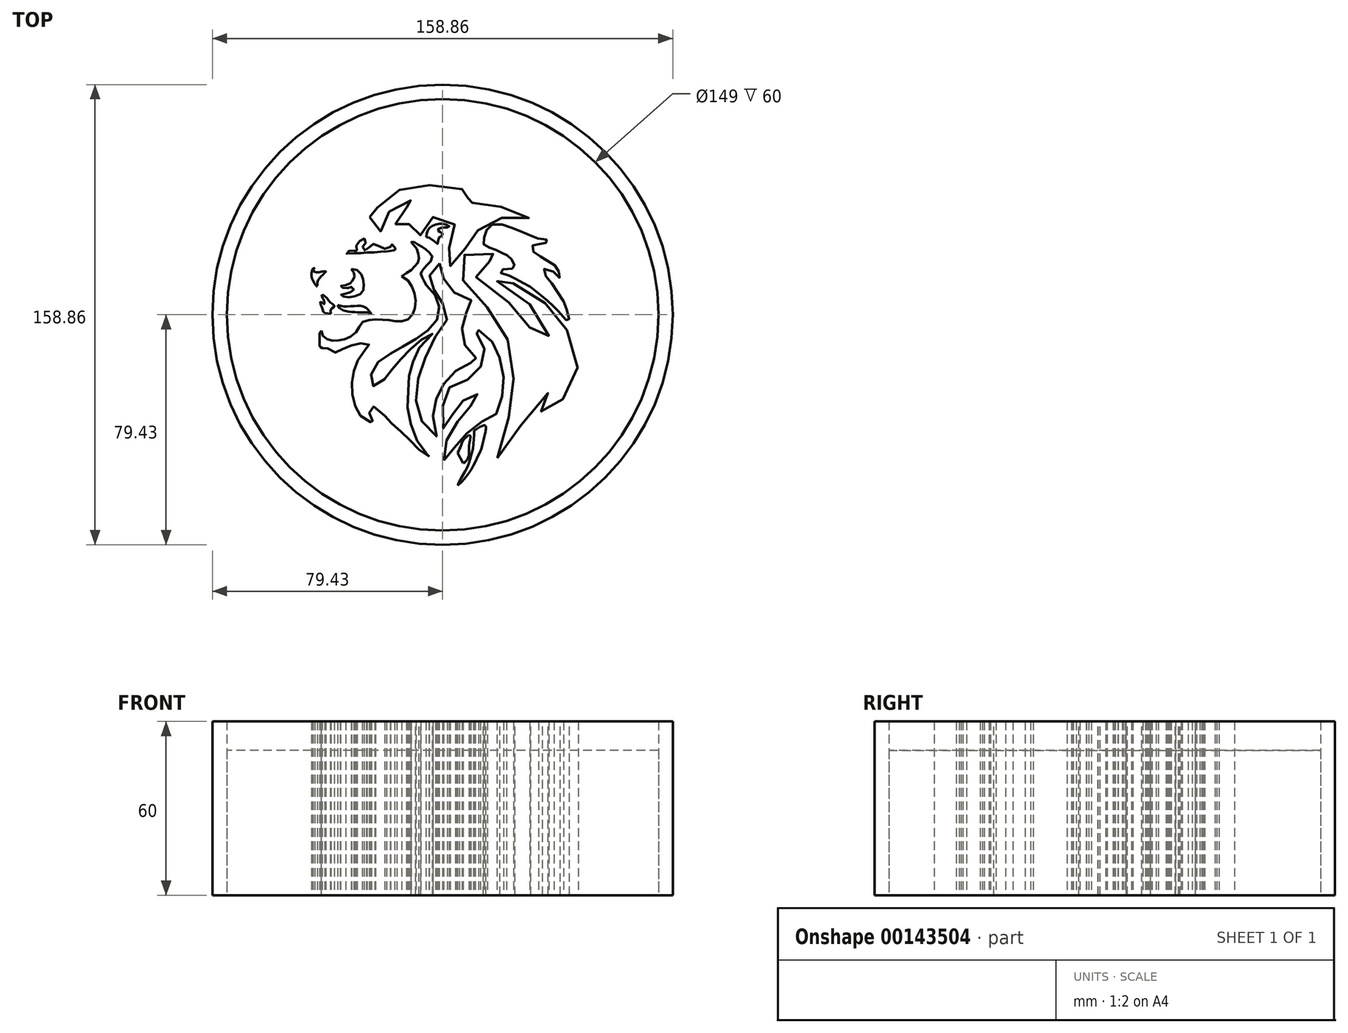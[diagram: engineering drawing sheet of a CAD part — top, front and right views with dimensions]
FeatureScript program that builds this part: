
annotation { "Feature Type Name" : "Feature", "Feature Type Description" : "" }
export const myFeature = defineFeature(function(context is Context, id is Id, definition is map)
    precondition{}
    {
        {
            var Q0;
            Q0=qCreatedBy(makeId("Top.planeOp"),FACE);
            var sketch = newSketch(context, id + "F0", { "sketchPlane" : qUnion([Q0])});
            skCircle(sketch, "E0", {"center": v(0, 0) * mm, "radius": 74.5 * mm});
            skCircle(sketch, "E1", {"center": v(0, 0) * mm, "radius": 79.43 * mm});
            skSolve(sketch);
        }
        {
            var Q0;
            Q0=makeQuery(id+"F0.imprint","IMPRINT",FACE,{"disambiguationData":[TD([[makeQuery(id+"F0.imprint","IMPRINT",EDGE,{"derivedFrom":sQuery(id+"F0.wireOp",EDGE,"E0")}),1.0]])]});
            var sketch = newSketch(context, id + "F1", { "sketchPlane" : qUnion([Q0])});
            skPoint(sketch, "E2", {"position": v(-26.29, 25.3) * mm});
            skPoint(sketch, "E3", {"position": v(-27.08, 24.28) * mm});
            skPoint(sketch, "E4", {"position": v(-27.66, 23.4) * mm});
            skPoint(sketch, "E5", {"position": v(-27.51, 22.47) * mm});
            skPoint(sketch, "E6", {"position": v(-26.13, 22.33) * mm});
            skPoint(sketch, "E7", {"position": v(-25.18, 23.42) * mm});
            skPoint(sketch, "E8", {"position": v(-24.17, 24.44) * mm});
            skPoint(sketch, "E9", {"position": v(-22.71, 24.09) * mm});
            skPoint(sketch, "E10", {"position": v(-20.89, 23.22) * mm});
            skPoint(sketch, "E11", {"position": v(-19.43, 22.72) * mm});
            skPoint(sketch, "E12", {"position": v(-17.97, 23.53) * mm});
            skPoint(sketch, "E13", {"position": v(-17.97, 24.4) * mm});
            skPoint(sketch, "E14", {"position": v(-17.1, 23.97) * mm});
            skPoint(sketch, "E15", {"position": v(-16.44, 23.02) * mm});
            skPoint(sketch, "E16", {"position": v(-15.71, 22.66) * mm});
            skPoint(sketch, "E17", {"position": v(-17.38, 22.15) * mm});
            skPoint(sketch, "E18", {"position": v(-19.57, 21.92) * mm});
            skPoint(sketch, "E19", {"position": v(-21.39, 21.77) * mm});
            skPoint(sketch, "E20", {"position": v(-23.43, 21.54) * mm});
            skPoint(sketch, "E21", {"position": v(-25.83, 21.53) * mm});
            skPoint(sketch, "E22", {"position": v(-27.8, 21.3) * mm});
            skPoint(sketch, "E23", {"position": v(-29.54, 21.22) * mm});
            skPoint(sketch, "E24", {"position": v(-31.73, 21.2) * mm});
            skPoint(sketch, "E25", {"position": v(-33.48, 21.2) * mm});
            skPoint(sketch, "E26", {"position": v(-31.73, 22.16) * mm});
            skPoint(sketch, "E27", {"position": v(-29.55, 22.24) * mm});
            skPoint(sketch, "E28", {"position": v(-29.85, 23.47) * mm});
            skPoint(sketch, "E29", {"position": v(-29.2, 24.78) * mm});
            skPoint(sketch, "E30", {"position": v(-28.04, 25.95) * mm});
            skPoint(sketch, "E31", {"position": v(-26.95, 26.32) * mm});
            skFitSpline(sketch, "E32", {"points": [v(-26.95, 26.32) * mm, v(-26.29, 25.3) * mm, v(-27.08, 24.28) * mm, v(-27.66, 23.4) * mm, v(-27.51, 22.47) * mm, v(-26.13, 22.33) * mm, v(-25.18, 23.42) * mm, v(-24.17, 24.44) * mm, v(-22.71, 24.09) * mm, v(-20.89, 23.22) * mm, v(-19.43, 22.72) * mm, v(-17.97, 23.53) * mm, v(-17.97, 24.4) * mm, v(-17.1, 23.97) * mm, v(-16.44, 23.02) * mm, v(-15.71, 22.66) * mm, v(-17.38, 22.15) * mm, v(-19.57, 21.92) * mm, v(-21.39, 21.77) * mm, v(-23.43, 21.54) * mm, v(-25.83, 21.53) * mm, v(-27.8, 21.3) * mm, v(-29.54, 21.22) * mm, v(-31.73, 21.2) * mm, v(-33.48, 21.2) * mm, v(-31.73, 22.16) * mm, v(-29.55, 22.24) * mm, v(-29.85, 23.47) * mm, v(-29.2, 24.78) * mm, v(-28.04, 25.95) * mm, v(-26.95, 26.32) * mm]});
            skPoint(sketch, "E33", {"position": v(-31.49, 15.76) * mm});
            skPoint(sketch, "E34", {"position": v(-29.68, 15.5) * mm});
            skPoint(sketch, "E35", {"position": v(-28.25, 14.2) * mm});
            skPoint(sketch, "E36", {"position": v(-27.6, 12.78) * mm});
            skPoint(sketch, "E37", {"position": v(-27.15, 11.31) * mm});
            skPoint(sketch, "E38", {"position": v(-27.25, 9.4) * mm});
            skPoint(sketch, "E39", {"position": v(-27.79, 7.88) * mm});
            skPoint(sketch, "E40", {"position": v(-28.82, 6.84) * mm});
            skPoint(sketch, "E41", {"position": v(-30.73, 6.28) * mm});
            skPoint(sketch, "E42", {"position": v(-32.75, 6.06) * mm});
            skPoint(sketch, "E43", {"position": v(-34.44, 6.32) * mm});
            skPoint(sketch, "E44", {"position": v(-35.15, 6.7) * mm});
            skPoint(sketch, "E45", {"position": v(-34.28, 7.25) * mm});
            skPoint(sketch, "E46", {"position": v(-33.03, 7.25) * mm});
            skPoint(sketch, "E47", {"position": v(-31.66, 7.8) * mm});
            skPoint(sketch, "E48", {"position": v(-30.8, 8.52) * mm});
            skPoint(sketch, "E49", {"position": v(-30.69, 9.12) * mm});
            skPoint(sketch, "E50", {"position": v(-31.5, 9.6) * mm});
            skPoint(sketch, "E51", {"position": v(-32.33, 9.27) * mm});
            skPoint(sketch, "E52", {"position": v(-33.47, 9.21) * mm});
            skPoint(sketch, "E53", {"position": v(-34.56, 9.37) * mm});
            skPoint(sketch, "E54", {"position": v(-35.27, 9.86) * mm});
            skPoint(sketch, "E55", {"position": v(-34.3, 10.19) * mm});
            skPoint(sketch, "E56", {"position": v(-33.1, 10.3) * mm});
            skPoint(sketch, "E57", {"position": v(-31.9, 10.85) * mm});
            skPoint(sketch, "E58", {"position": v(-31.3, 11.51) * mm});
            skPoint(sketch, "E59", {"position": v(-30.7, 12.28) * mm});
            skPoint(sketch, "E60", {"position": v(-30.43, 13.26) * mm});
            skPoint(sketch, "E61", {"position": v(-30.44, 13.97) * mm});
            skPoint(sketch, "E62", {"position": v(-30.93, 14.94) * mm});
            skPoint(sketch, "E63", {"position": v(-36.17, 3.32) * mm});
            skPoint(sketch, "E64", {"position": v(-35.08, 3) * mm});
            skPoint(sketch, "E65", {"position": v(-33.6, 2.84) * mm});
            skPoint(sketch, "E66", {"position": v(-32.13, 2.96) * mm});
            skPoint(sketch, "E67", {"position": v(-30.5, 3.02) * mm});
            skPoint(sketch, "E68", {"position": v(-28.91, 3.19) * mm});
            skPoint(sketch, "E69", {"position": v(-27.77, 3.03) * mm});
            skPoint(sketch, "E70", {"position": v(-26.56, 2.44) * mm});
            skPoint(sketch, "E71", {"position": v(-25.8, 1.79) * mm});
            skPoint(sketch, "E72", {"position": v(-25.14, 1.14) * mm});
            skPoint(sketch, "E73", {"position": v(-24.59, 0.49) * mm});
            skPoint(sketch, "E74", {"position": v(-25.85, 0.8) * mm});
            skPoint(sketch, "E75", {"position": v(-27.1, 0.8) * mm});
            skPoint(sketch, "E76", {"position": v(-28.74, 0.85) * mm});
            skPoint(sketch, "E77", {"position": v(-30.05, 0.9) * mm});
            skPoint(sketch, "E78", {"position": v(-31.25, 0.9) * mm});
            skPoint(sketch, "E79", {"position": v(-32.72, 1.16) * mm});
            skPoint(sketch, "E80", {"position": v(-33.98, 1.42) * mm});
            skPoint(sketch, "E81", {"position": v(-35.02, 1.8) * mm});
            skPoint(sketch, "E82", {"position": v(-37.32, 3.03) * mm});
            skPoint(sketch, "E83", {"position": v(-38.03, 3.7) * mm});
            skPoint(sketch, "E84", {"position": v(-38.85, 4.34) * mm});
            skPoint(sketch, "E85", {"position": v(-39.57, 5.32) * mm});
            skPoint(sketch, "E86", {"position": v(-40.22, 6.02) * mm});
            skPoint(sketch, "E87", {"position": v(-41, 6.62) * mm});
            skPoint(sketch, "E88", {"position": v(-41.6, 7) * mm});
            skPoint(sketch, "E89", {"position": v(-41.59, 6.02) * mm});
            skPoint(sketch, "E90", {"position": v(-40.93, 5.2) * mm});
            skPoint(sketch, "E91", {"position": v(-40.76, 4.17) * mm});
            skPoint(sketch, "E92", {"position": v(-40.76, 3.68) * mm});
            skPoint(sketch, "E93", {"position": v(-41.58, 4.17) * mm});
            skPoint(sketch, "E94", {"position": v(-42.13, 4.5) * mm});
            skPoint(sketch, "E95", {"position": v(-42.13, 3.72) * mm});
            skPoint(sketch, "E96", {"position": v(-41.74, 2.76) * mm});
            skPoint(sketch, "E97", {"position": v(-41.47, 2.04) * mm});
            skPoint(sketch, "E98", {"position": v(-41.12, 1.08) * mm});
            skPoint(sketch, "E99", {"position": v(-40.57, 0.53) * mm});
            skPoint(sketch, "E100", {"position": v(-38.5, 0.37) * mm});
            skPoint(sketch, "E101", {"position": v(-38.6, 0.85) * mm});
            skPoint(sketch, "E102", {"position": v(-38.71, 1.47) * mm});
            skPoint(sketch, "E103", {"position": v(-38.61, 1.74) * mm});
            skPoint(sketch, "E104", {"position": v(-38.37, 2.05) * mm});
            skPoint(sketch, "E105", {"position": v(-37.9, 2.43) * mm});
            skPoint(sketch, "E106", {"position": v(-43.32, 9.75) * mm});
            skPoint(sketch, "E107", {"position": v(-43.16, 10.5) * mm});
            skPoint(sketch, "E108", {"position": v(-43.13, 11.43) * mm});
            skPoint(sketch, "E109", {"position": v(-42.79, 12.26) * mm});
            skPoint(sketch, "E110", {"position": v(-42.3, 12.88) * mm});
            skPoint(sketch, "E111", {"position": v(-41.7, 13.46) * mm});
            skPoint(sketch, "E112", {"position": v(-41.18, 13.88) * mm});
            skPoint(sketch, "E113", {"position": v(-40.73, 14.46) * mm});
            skPoint(sketch, "E114", {"position": v(-40.25, 15.01) * mm});
            skPoint(sketch, "E115", {"position": v(-41.08, 15) * mm});
            skPoint(sketch, "E116", {"position": v(-42.14, 14.76) * mm});
            skPoint(sketch, "E117", {"position": v(-43.35, 14.62) * mm});
            skPoint(sketch, "E118", {"position": v(-44.28, 14.86) * mm});
            skPoint(sketch, "E119", {"position": v(-44.7, 15.37) * mm});
            skPoint(sketch, "E120", {"position": v(-44.62, 15.99) * mm});
            skPoint(sketch, "E121", {"position": v(-44.04, 16.37) * mm});
            skPoint(sketch, "E122", {"position": v(-45.04, 15.37) * mm});
            skPoint(sketch, "E123", {"position": v(-45.24, 14.3) * mm});
            skPoint(sketch, "E124", {"position": v(-45.27, 13.24) * mm});
            skPoint(sketch, "E125", {"position": v(-44.92, 12.21) * mm});
            skPoint(sketch, "E126", {"position": v(-44.5, 11.36) * mm});
            skFitSpline(sketch, "E127", {"points": [v(-44.04, 16.37) * mm, v(-44.62, 15.99) * mm, v(-45.04, 15.37) * mm, v(-45.24, 14.3) * mm, v(-45.27, 13.24) * mm, v(-44.92, 12.21) * mm, v(-44.5, 11.36) * mm, v(-43.32, 9.75) * mm, v(-43.16, 10.5) * mm, v(-43.13, 11.43) * mm, v(-42.79, 12.26) * mm, v(-42.3, 12.88) * mm, v(-41.7, 13.46) * mm, v(-41.18, 13.88) * mm, v(-40.73, 14.46) * mm, v(-40.25, 15.01) * mm, v(-41.08, 15) * mm, v(-42.14, 14.76) * mm, v(-43.35, 14.62) * mm, v(-44.28, 14.86) * mm, v(-44.7, 15.37) * mm, v(-44.04, 16.37) * mm]});
            skFitSpline(sketch, "E128", {"points": [v(-31.49, 15.76) * mm, v(-30.93, 14.94) * mm, v(-30.44, 13.97) * mm, v(-30.43, 13.26) * mm, v(-30.7, 12.28) * mm, v(-31.3, 11.51) * mm, v(-31.9, 10.85) * mm, v(-33.1, 10.3) * mm, v(-34.3, 10.19) * mm, v(-35.27, 9.86) * mm, v(-34.56, 9.37) * mm, v(-33.47, 9.21) * mm, v(-32.33, 9.27) * mm, v(-31.5, 9.6) * mm, v(-30.69, 9.12) * mm, v(-30.8, 8.52) * mm, v(-31.66, 7.8) * mm, v(-33.03, 7.25) * mm, v(-34.28, 7.25) * mm, v(-35.15, 6.7) * mm, v(-34.44, 6.32) * mm, v(-32.75, 6.06) * mm, v(-30.73, 6.28) * mm, v(-28.82, 6.84) * mm, v(-27.55, 7.88) * mm, v(-27.25, 9.4) * mm, v(-27.15, 11.31) * mm, v(-27.6, 12.78) * mm, v(-28.25, 14.2) * mm, v(-29.68, 15.5) * mm, v(-31.49, 15.76) * mm]});
            skFitSpline(sketch, "E129", {"points": [v(-38.5, 0.37) * mm, v(-38.6, 0.85) * mm, v(-38.71, 1.47) * mm, v(-38.61, 1.74) * mm, v(-38.37, 2.05) * mm, v(-37.9, 2.43) * mm, v(-37.32, 3.03) * mm, v(-38.03, 3.7) * mm, v(-38.85, 4.34) * mm, v(-39.57, 5.32) * mm, v(-40.22, 6.02) * mm, v(-41, 6.62) * mm, v(-41.6, 7) * mm, v(-41.59, 6.02) * mm, v(-40.93, 5.2) * mm, v(-40.76, 4.17) * mm, v(-40.76, 3.68) * mm, v(-41.58, 4.17) * mm, v(-42.13, 4.5) * mm, v(-42.13, 3.72) * mm, v(-41.74, 2.76) * mm, v(-41.47, 2.04) * mm, v(-41.12, 1.08) * mm, v(-40.57, 0.53) * mm], "startDerivative": vector(-2.7, 13.07) * mm, "endDerivative": vector(14.2, -10.78) * mm});
            skLineSegment(sketch, "E130", {"start": v(-40.57, 0.53) * mm, "end": v(-38.5, 0.37) * mm});
            skFitSpline(sketch, "E131", {"points": [v(-36.17, 3.32) * mm, v(-35.08, 3) * mm, v(-33.6, 2.84) * mm, v(-32.13, 2.96) * mm, v(-30.5, 3.02) * mm, v(-28.91, 3.19) * mm, v(-27.77, 3.03) * mm, v(-26.56, 2.44) * mm, v(-25.8, 1.79) * mm, v(-25.14, 1.14) * mm, v(-24.59, 0.49) * mm, v(-25.85, 0.8) * mm, v(-27.1, 0.8) * mm, v(-28.74, 0.85) * mm, v(-30.05, 0.9) * mm, v(-31.25, 0.9) * mm, v(-32.72, 1.16) * mm, v(-33.98, 1.42) * mm, v(-35.02, 1.8) * mm, v(-36.17, 3.32) * mm]});
            skPoint(sketch, "E132", {"position": v(-41.77, -5.54) * mm});
            skPoint(sketch, "E133", {"position": v(-41.77, -6.47) * mm});
            skPoint(sketch, "E134", {"position": v(-41.15, -7.5) * mm});
            skPoint(sketch, "E135", {"position": v(-40.33, -8.27) * mm});
            skPoint(sketch, "E136", {"position": v(-39.5, -8.63) * mm});
            skPoint(sketch, "E137", {"position": v(-38.27, -8.94) * mm});
            skPoint(sketch, "E138", {"position": v(-37.14, -8.94) * mm});
            skPoint(sketch, "E139", {"position": v(-35.75, -8.89) * mm});
            skPoint(sketch, "E140", {"position": v(-34.56, -8.68) * mm});
            skPoint(sketch, "E141", {"position": v(-33.27, -8.22) * mm});
            skPoint(sketch, "E142", {"position": v(-32.04, -7.65) * mm});
            skPoint(sketch, "E143", {"position": v(-30.7, -6.78) * mm});
            skPoint(sketch, "E144", {"position": v(-29.57, -5.7) * mm});
            skPoint(sketch, "E145", {"position": v(-28.74, -4.25) * mm});
            skPoint(sketch, "E146", {"position": v(-28.48, -2.96) * mm});
            skPoint(sketch, "E147", {"position": v(-27.1, -2.35) * mm});
            skPoint(sketch, "E148", {"position": v(-25.75, -1.88) * mm});
            skPoint(sketch, "E149", {"position": v(-24.2, -1.63) * mm});
            skPoint(sketch, "E150", {"position": v(-22.56, -1.57) * mm});
            skPoint(sketch, "E151", {"position": v(-21.02, -1.68) * mm});
            skPoint(sketch, "E152", {"position": v(-19.37, -1.83) * mm});
            skPoint(sketch, "E153", {"position": v(-17.87, -1.93) * mm});
            skPoint(sketch, "E154", {"position": v(-16.59, -2.14) * mm});
            skPoint(sketch, "E155", {"position": v(-15.1, -2.24) * mm});
            skPoint(sketch, "E156", {"position": v(-13.7, -2.24) * mm});
            skPoint(sketch, "E157", {"position": v(-12.47, -1.88) * mm});
            skPoint(sketch, "E158", {"position": v(-11.18, -0.96) * mm});
            skPoint(sketch, "E159", {"position": v(-10.1, 0.7) * mm});
            skPoint(sketch, "E160", {"position": v(-9.63, 2.08) * mm});
            skPoint(sketch, "E161", {"position": v(-9.38, 3.83) * mm});
            skPoint(sketch, "E162", {"position": v(-9.33, 5.48) * mm});
            skPoint(sketch, "E163", {"position": v(-9.74, 7.34) * mm});
            skPoint(sketch, "E164", {"position": v(-10.4, 9.19) * mm});
            skPoint(sketch, "E165", {"position": v(-11.18, 10.79) * mm});
            skPoint(sketch, "E166", {"position": v(-12.42, 12.23) * mm});
            skPoint(sketch, "E167", {"position": v(-14.12, 13.2) * mm});
            skPoint(sketch, "E168", {"position": v(-12.42, 14.4) * mm});
            skPoint(sketch, "E169", {"position": v(-10.82, 15.47) * mm});
            skPoint(sketch, "E170", {"position": v(-9.48, 16.86) * mm});
            skPoint(sketch, "E171", {"position": v(-8.3, 18.4) * mm});
            skPoint(sketch, "E172", {"position": v(-8.3, 20.37) * mm});
            skPoint(sketch, "E173", {"position": v(-8.66, 22.17) * mm});
            skPoint(sketch, "E174", {"position": v(-9.9, 24.02) * mm});
            skPoint(sketch, "E175", {"position": v(-10.77, 24.9) * mm});
            skPoint(sketch, "E176", {"position": v(-10.66, 25.41) * mm});
            skPoint(sketch, "E177", {"position": v(-9.17, 24.64) * mm});
            skPoint(sketch, "E178", {"position": v(-7.52, 23.76) * mm});
            skPoint(sketch, "E179", {"position": v(-6.13, 22.79) * mm});
            skPoint(sketch, "E180", {"position": v(-4.84, 21.7) * mm});
            skPoint(sketch, "E181", {"position": v(-3.56, 20.26) * mm});
            skPoint(sketch, "E182", {"position": v(-4.28, 18.25) * mm});
            skPoint(sketch, "E183", {"position": v(-5.82, 16.7) * mm});
            skPoint(sketch, "E184", {"position": v(-6.65, 15.73) * mm});
            skPoint(sketch, "E185", {"position": v(-7.37, 14.75) * mm});
            skPoint(sketch, "E186", {"position": v(-7.52, 14.19) * mm});
            skPoint(sketch, "E187", {"position": v(-7.21, 13.3) * mm});
            skPoint(sketch, "E188", {"position": v(-6.54, 11.92) * mm});
            skPoint(sketch, "E189", {"position": v(-5.82, 10.53) * mm});
            skPoint(sketch, "E190", {"position": v(-4.84, 9.34) * mm});
            skPoint(sketch, "E191", {"position": v(-3.5, 7.85) * mm});
            skPoint(sketch, "E192", {"position": v(-2.42, 6.46) * mm});
            skPoint(sketch, "E193", {"position": v(-1.65, 5.17) * mm});
            skPoint(sketch, "E194", {"position": v(-1.14, 3.73) * mm});
            skPoint(sketch, "E195", {"position": v(-1.3, 1.93) * mm});
            skPoint(sketch, "E196", {"position": v(-1.3, -0.39) * mm});
            skPoint(sketch, "E197", {"position": v(-2.17, -2.14) * mm});
            skPoint(sketch, "E198", {"position": v(-3.4, -3.79) * mm});
            skPoint(sketch, "E199", {"position": v(-5.36, -5.6) * mm});
            skPoint(sketch, "E200", {"position": v(-6.9, -6.88) * mm});
            skPoint(sketch, "E201", {"position": v(-9.22, -8.32) * mm});
            skPoint(sketch, "E202", {"position": v(-12.1, -9.97) * mm});
            skPoint(sketch, "E203", {"position": v(-14.06, -11.2) * mm});
            skPoint(sketch, "E204", {"position": v(-16.07, -12.29) * mm});
            skPoint(sketch, "E205", {"position": v(-17.98, -13.42) * mm});
            skPoint(sketch, "E206", {"position": v(-19.93, -14.7) * mm});
            skPoint(sketch, "E207", {"position": v(-22.25, -16.36) * mm});
            skPoint(sketch, "E208", {"position": v(-23.85, -18.47) * mm});
            skPoint(sketch, "E209", {"position": v(-24.67, -20.63) * mm});
            skPoint(sketch, "E210", {"position": v(-24.88, -23.36) * mm});
            skPoint(sketch, "E211", {"position": v(-24.42, -24.5) * mm});
            skPoint(sketch, "E212", {"position": v(-22.77, -24.5) * mm});
            skPoint(sketch, "E213", {"position": v(-21.02, -23.41) * mm});
            skPoint(sketch, "E214", {"position": v(-19.68, -21.6) * mm});
            skPoint(sketch, "E215", {"position": v(-18.65, -20.01) * mm});
            skPoint(sketch, "E216", {"position": v(-17.51, -18.93) * mm});
            skPoint(sketch, "E217", {"position": v(-16.23, -17.54) * mm});
            skPoint(sketch, "E218", {"position": v(-14.73, -15.63) * mm});
            skPoint(sketch, "E219", {"position": v(-12.88, -13.68) * mm});
            skPoint(sketch, "E220", {"position": v(-11.64, -12.34) * mm});
            skPoint(sketch, "E221", {"position": v(-9.94, -10.9) * mm});
            skPoint(sketch, "E222", {"position": v(-7.99, -9.15) * mm});
            skPoint(sketch, "E223", {"position": v(-5.82, -7.7) * mm});
            skPoint(sketch, "E224", {"position": v(-3.3, -6.36) * mm});
            skPoint(sketch, "E225", {"position": v(-6.08, -8.78) * mm});
            skPoint(sketch, "E226", {"position": v(-8.09, -11.46) * mm});
            skPoint(sketch, "E227", {"position": v(-9.22, -13.83) * mm});
            skPoint(sketch, "E228", {"position": v(-10.25, -16.3) * mm});
            skPoint(sketch, "E229", {"position": v(-10.97, -18.62) * mm});
            skPoint(sketch, "E230", {"position": v(-11.64, -21.35) * mm});
            skPoint(sketch, "E231", {"position": v(-11.9, -23.46) * mm});
            skPoint(sketch, "E232", {"position": v(-11.9, -26.7) * mm});
            skPoint(sketch, "E233", {"position": v(-12.2, -29.9) * mm});
            skPoint(sketch, "E234", {"position": v(-11.9, -33.04) * mm});
            skPoint(sketch, "E235", {"position": v(-11.33, -36.34) * mm});
            skPoint(sketch, "E236", {"position": v(-10.4, -39.9) * mm});
            skPoint(sketch, "E237", {"position": v(-8.91, -43.24) * mm});
            skPoint(sketch, "E238", {"position": v(-7.37, -45.92) * mm});
            skPoint(sketch, "E239", {"position": v(-5.62, -47.87) * mm});
            skPoint(sketch, "E240", {"position": v(-4.64, -48.96) * mm});
            skPoint(sketch, "E241", {"position": v(-7.52, -47.1) * mm});
            skPoint(sketch, "E242", {"position": v(-10.51, -44.11) * mm});
            skPoint(sketch, "E243", {"position": v(-13.34, -41.33) * mm});
            skPoint(sketch, "E244", {"position": v(-16.38, -38.5) * mm});
            skPoint(sketch, "E245", {"position": v(-18.6, -36.6) * mm});
            skPoint(sketch, "E246", {"position": v(-20.66, -34.12) * mm});
            skPoint(sketch, "E247", {"position": v(-24.36, -31.7) * mm});
            skPoint(sketch, "E248", {"position": v(-25.24, -33.14) * mm});
            skPoint(sketch, "E249", {"position": v(-25.09, -35.05) * mm});
            skPoint(sketch, "E250", {"position": v(-24.16, -36.75) * mm});
            skPoint(sketch, "E251", {"position": v(-23.39, -37.52) * mm});
            skPoint(sketch, "E252", {"position": v(-26.42, -36.39) * mm});
            skPoint(sketch, "E253", {"position": v(-28.43, -34.69) * mm});
            skPoint(sketch, "E254", {"position": v(-29.82, -32.37) * mm});
            skPoint(sketch, "E255", {"position": v(-30.96, -28.61) * mm});
            skPoint(sketch, "E256", {"position": v(-31.32, -25.57) * mm});
            skPoint(sketch, "E257", {"position": v(-31.16, -21.71) * mm});
            skPoint(sketch, "E258", {"position": v(-30.5, -18.83) * mm});
            skPoint(sketch, "E259", {"position": v(-29.2, -15.63) * mm});
            skPoint(sketch, "E260", {"position": v(-27.2, -12.54) * mm});
            skPoint(sketch, "E261", {"position": v(-24.83, -10.43) * mm});
            skPoint(sketch, "E262", {"position": v(-25.96, -10.28) * mm});
            skPoint(sketch, "E263", {"position": v(-27.3, -9.92) * mm});
            skPoint(sketch, "E264", {"position": v(-29.93, -10.07) * mm});
            skPoint(sketch, "E265", {"position": v(-31.93, -10.74) * mm});
            skPoint(sketch, "E266", {"position": v(-34.1, -11.62) * mm});
            skPoint(sketch, "E267", {"position": v(-35.33, -12.34) * mm});
            skPoint(sketch, "E268", {"position": v(-36.83, -13.06) * mm});
            skPoint(sketch, "E269", {"position": v(-38.63, -12.18) * mm});
            skPoint(sketch, "E270", {"position": v(-39.97, -11.41) * mm});
            skPoint(sketch, "E271", {"position": v(-40.54, -11.26) * mm});
            skPoint(sketch, "E272", {"position": v(-41.62, -11.51) * mm});
            skPoint(sketch, "E273", {"position": v(-42.44, -10.84) * mm});
            skPoint(sketch, "E274", {"position": v(-42.44, -6.31) * mm});
            skFitSpline(sketch, "E275", {"points": [v(-41.77, -5.54) * mm, v(-41.77, -6.47) * mm, v(-41.15, -7.5) * mm, v(-40.33, -8.27) * mm, v(-39.5, -8.63) * mm, v(-38.27, -8.94) * mm, v(-37.14, -8.94) * mm, v(-35.75, -8.89) * mm, v(-34.56, -8.68) * mm, v(-33.27, -8.22) * mm, v(-32.04, -7.65) * mm, v(-30.7, -6.78) * mm, v(-29.57, -5.7) * mm, v(-28.74, -4.25) * mm, v(-28.48, -2.96) * mm, v(-27.1, -2.35) * mm, v(-25.75, -1.88) * mm, v(-24.2, -1.63) * mm, v(-22.56, -1.57) * mm, v(-21.02, -1.68) * mm, v(-19.37, -1.83) * mm, v(-17.87, -1.93) * mm, v(-16.59, -2.14) * mm, v(-15.1, -2.24) * mm, v(-13.7, -2.24) * mm, v(-12.47, -1.88) * mm, v(-11.18, -0.96) * mm, v(-10.1, 0.7) * mm, v(-9.63, 2.08) * mm, v(-9.38, 3.83) * mm, v(-9.33, 5.48) * mm, v(-9.74, 7.34) * mm, v(-10.4, 9.19) * mm, v(-11.18, 10.79) * mm, v(-12.42, 12.23) * mm, v(-14.12, 13.2) * mm], "startDerivative": vector(-5.46, -40.92) * mm, "endDerivative": vector(-54.42, 26.15) * mm});
            skLineSegment(sketch, "E276", {"start": v(-14.12, 13.2) * mm, "end": v(-12.42, 14.4) * mm});
            skLineSegment(sketch, "E277", {"start": v(-12.42, 14.4) * mm, "end": v(-10.82, 15.47) * mm});
            skFitSpline(sketch, "E278", {"points": [v(-10.82, 15.47) * mm, v(-9.48, 16.86) * mm, v(-8.3, 18.4) * mm, v(-8.3, 20.37) * mm, v(-8.66, 22.17) * mm, v(-9.9, 24.02) * mm, v(-10.77, 24.9) * mm, v(-10.66, 25.41) * mm, v(-9.17, 24.64) * mm, v(-7.52, 23.76) * mm, v(-6.13, 22.79) * mm, v(-4.84, 21.7) * mm, v(-3.56, 20.26) * mm, v(-4.28, 18.25) * mm, v(-5.82, 16.7) * mm, v(-6.65, 15.73) * mm, v(-7.37, 14.75) * mm, v(-7.52, 14.19) * mm, v(-7.21, 13.3) * mm, v(-6.54, 11.92) * mm, v(-5.82, 10.53) * mm, v(-4.84, 9.34) * mm, v(-3.5, 7.85) * mm, v(-2.42, 6.46) * mm], "startDerivative": vector(27.06, 28.76) * mm, "endDerivative": vector(22.35, -29.94) * mm});
            skPoint(sketch, "E279", {"position": v(-2.2, -42.17) * mm});
            skPoint(sketch, "E280", {"position": v(-5.83, -39.06) * mm});
            skPoint(sketch, "E281", {"position": v(-7.78, -35.03) * mm});
            skPoint(sketch, "E282", {"position": v(-9.08, -30.62) * mm});
            skPoint(sketch, "E283", {"position": v(-8.69, -25.82) * mm});
            skPoint(sketch, "E284", {"position": v(-8.3, -21.4) * mm});
            skPoint(sketch, "E285", {"position": v(-6.87, -17.13) * mm});
            skPoint(sketch, "E286", {"position": v(-5.31, -13.1) * mm});
            skPoint(sketch, "E287", {"position": v(-2.98, -8.3) * mm});
            skPoint(sketch, "E288", {"position": v(0, -4.15) * mm});
            skPoint(sketch, "E289", {"position": v(1.57, -1.42) * mm});
            skPoint(sketch, "E290", {"position": v(0.92, 1.82) * mm});
            skPoint(sketch, "E291", {"position": v(0, 4.01) * mm});
            skPoint(sketch, "E292", {"position": v(-1.04, 5.97) * mm});
            skPoint(sketch, "E293", {"position": v(-2.51, 8) * mm});
            skPoint(sketch, "E294", {"position": v(-3.86, 9.7) * mm});
            skPoint(sketch, "E295", {"position": v(-4.72, 11.8) * mm});
            skPoint(sketch, "E296", {"position": v(-4.17, 14.3) * mm});
            skPoint(sketch, "E297", {"position": v(-2.82, 16.26) * mm});
            skPoint(sketch, "E298", {"position": v(-1.04, 17.67) * mm});
            skPoint(sketch, "E299", {"position": v(-0.61, 15.53) * mm});
            skPoint(sketch, "E300", {"position": v(0, 13.2) * mm});
            skPoint(sketch, "E301", {"position": v(1.47, 10.87) * mm});
            skPoint(sketch, "E302", {"position": v(3.24, 8.55) * mm});
            skPoint(sketch, "E303", {"position": v(4.9, 6.9) * mm});
            skPoint(sketch, "E304", {"position": v(7.53, 5.48) * mm});
            skPoint(sketch, "E305", {"position": v(10.96, 4.5) * mm});
            skPoint(sketch, "E306", {"position": v(9.18, 2.18) * mm});
            skPoint(sketch, "E307", {"position": v(7.9, 0) * mm});
            skPoint(sketch, "E308", {"position": v(7.04, -2.79) * mm});
            skPoint(sketch, "E309", {"position": v(6.73, -5.48) * mm});
            skPoint(sketch, "E310", {"position": v(7.04, -8.05) * mm});
            skPoint(sketch, "E311", {"position": v(7.84, -10.69) * mm});
            skPoint(sketch, "E312", {"position": v(8.94, -12.95) * mm});
            skPoint(sketch, "E313", {"position": v(11.39, -14.91) * mm});
            skPoint(sketch, "E314", {"position": v(13.04, -15.77) * mm});
            skPoint(sketch, "E315", {"position": v(11.08, -16.26) * mm});
            skPoint(sketch, "E316", {"position": v(8.7, -17.06) * mm});
            skPoint(sketch, "E317", {"position": v(6.3, -18.28) * mm});
            skPoint(sketch, "E318", {"position": v(3.61, -20.12) * mm});
            skPoint(sketch, "E319", {"position": v(1.47, -22.38) * mm});
            skPoint(sketch, "E320", {"position": v(0, -24.59) * mm});
            skPoint(sketch, "E321", {"position": v(-1.41, -26.8) * mm});
            skPoint(sketch, "E322", {"position": v(-2.33, -29.49) * mm});
            skPoint(sketch, "E323", {"position": v(-3.06, -32.37) * mm});
            skPoint(sketch, "E324", {"position": v(-3.3, -35) * mm});
            skPoint(sketch, "E325", {"position": v(-3, -37.94) * mm});
            skPoint(sketch, "E326", {"position": v(0.49, -39.47) * mm});
            skPoint(sketch, "E327", {"position": v(0, -36.72) * mm});
            skPoint(sketch, "E328", {"position": v(0, -32.86) * mm});
            skPoint(sketch, "E329", {"position": v(0.31, -30.57) * mm});
            skPoint(sketch, "E330", {"position": v(0.97, -27.99) * mm});
            skPoint(sketch, "E331", {"position": v(2.13, -25.55) * mm});
            skPoint(sketch, "E332", {"position": v(3.88, -23.5) * mm});
            skPoint(sketch, "E333", {"position": v(7.05, -23.07) * mm});
            skPoint(sketch, "E334", {"position": v(9.42, -21.87) * mm});
            skPoint(sketch, "E335", {"position": v(11.5, -20.3) * mm});
            skPoint(sketch, "E336", {"position": v(12.84, -18.48) * mm});
            skPoint(sketch, "E337", {"position": v(13.9, -15.9) * mm});
            skPoint(sketch, "E338", {"position": v(14.37, -14.04) * mm});
            skPoint(sketch, "E339", {"position": v(14.44, -11.85) * mm});
            skPoint(sketch, "E340", {"position": v(13.93, -9.7) * mm});
            skPoint(sketch, "E341", {"position": v(12.8, -7.85) * mm});
            skPoint(sketch, "E342", {"position": v(11.67, -6.46) * mm});
            skPoint(sketch, "E343", {"position": v(9.7, -5.04) * mm});
            skPoint(sketch, "E344", {"position": v(10.7, -4.68) * mm});
            skPoint(sketch, "E345", {"position": v(12.18, -5.15) * mm});
            skPoint(sketch, "E346", {"position": v(13.64, -6.03) * mm});
            skPoint(sketch, "E347", {"position": v(15.28, -7.27) * mm});
            skPoint(sketch, "E348", {"position": v(17.06, -9.34) * mm});
            skPoint(sketch, "E349", {"position": v(18.08, -11.09) * mm});
            skPoint(sketch, "E350", {"position": v(19, -13.16) * mm});
            skPoint(sketch, "E351", {"position": v(19.69, -15.1) * mm});
            skPoint(sketch, "E352", {"position": v(20.34, -17.72) * mm});
            skPoint(sketch, "E353", {"position": v(20.92, -20.56) * mm});
            skPoint(sketch, "E354", {"position": v(21.03, -23.22) * mm});
            skPoint(sketch, "E355", {"position": v(20.85, -26.02) * mm});
            skPoint(sketch, "E356", {"position": v(20.6, -28.06) * mm});
            skPoint(sketch, "E357", {"position": v(20.2, -30.1) * mm});
            skPoint(sketch, "E358", {"position": v(19.36, -32.54) * mm});
            skPoint(sketch, "E359", {"position": v(18.3, -34.72) * mm});
            skPoint(sketch, "E360", {"position": v(17.61, -35.74) * mm});
            skPoint(sketch, "E361", {"position": v(14.95, -36.36) * mm});
            skPoint(sketch, "E362", {"position": v(12.73, -37.38) * mm});
            skPoint(sketch, "E363", {"position": v(10.25, -39.06) * mm});
            skPoint(sketch, "E364", {"position": v(8.83, -40.48) * mm});
            skPoint(sketch, "E365", {"position": v(6.83, -42.52) * mm});
            skPoint(sketch, "E366", {"position": v(5.3, -44.41) * mm});
            skPoint(sketch, "E367", {"position": v(3.92, -46.16) * mm});
            skPoint(sketch, "E368", {"position": v(2.6, -47.69) * mm});
            skPoint(sketch, "E369", {"position": v(1.48, -49.25) * mm});
            skPoint(sketch, "E370", {"position": v(0.5, -50.24) * mm});
            skPoint(sketch, "E371", {"position": v(0.46, -47.87) * mm});
            skPoint(sketch, "E372", {"position": v(0.86, -45) * mm});
            skPoint(sketch, "E373", {"position": v(2.2, -41.46) * mm});
            skPoint(sketch, "E374", {"position": v(3.77, -38.8) * mm});
            skPoint(sketch, "E375", {"position": v(5.56, -36.47) * mm});
            skPoint(sketch, "E376", {"position": v(7.52, -34.07) * mm});
            skPoint(sketch, "E377", {"position": v(9.16, -32.17) * mm});
            skPoint(sketch, "E378", {"position": v(10.76, -30.28) * mm});
            skPoint(sketch, "E379", {"position": v(11.93, -28.6) * mm});
            skPoint(sketch, "E380", {"position": v(12.44, -27.59) * mm});
            skPoint(sketch, "E381", {"position": v(11.06, -27.62) * mm});
            skPoint(sketch, "E382", {"position": v(9.16, -28.13) * mm});
            skPoint(sketch, "E383", {"position": v(7.81, -28.9) * mm});
            skPoint(sketch, "E384", {"position": v(6.69, -30.03) * mm});
            skPoint(sketch, "E385", {"position": v(5.08, -31.63) * mm});
            skPoint(sketch, "E386", {"position": v(4.03, -33.41) * mm});
            skPoint(sketch, "E387", {"position": v(3, -35.27) * mm});
            skPoint(sketch, "E388", {"position": v(1.91, -37.35) * mm});
            skPoint(sketch, "E389", {"position": v(4.45, 15.9) * mm});
            skPoint(sketch, "E390", {"position": v(6.48, 12.61) * mm});
            skPoint(sketch, "E391", {"position": v(8.96, 9.43) * mm});
            skPoint(sketch, "E392", {"position": v(11.56, 6.89) * mm});
            skPoint(sketch, "E393", {"position": v(14.63, 3.3) * mm});
            skPoint(sketch, "E394", {"position": v(17.8, 0) * mm});
            skPoint(sketch, "E395", {"position": v(19.89, -3.52) * mm});
            skPoint(sketch, "E396", {"position": v(22.49, -8.66) * mm});
            skPoint(sketch, "E397", {"position": v(23.76, -13.98) * mm});
            skPoint(sketch, "E398", {"position": v(24.45, -18.66) * mm});
            skPoint(sketch, "E399", {"position": v(24.45, -23.4) * mm});
            skPoint(sketch, "E400", {"position": v(24, -28.26) * mm});
            skPoint(sketch, "E401", {"position": v(23.3, -33.35) * mm});
            skPoint(sketch, "E402", {"position": v(22.32, -37.68) * mm});
            skPoint(sketch, "E403", {"position": v(21.27, -42.02) * mm});
            skPoint(sketch, "E404", {"position": v(18.85, -49.53) * mm});
            skPoint(sketch, "E405", {"position": v(21.74, -45.89) * mm});
            skPoint(sketch, "E406", {"position": v(24.97, -41.32) * mm});
            skPoint(sketch, "E407", {"position": v(28.39, -36.24) * mm});
            skPoint(sketch, "E408", {"position": v(32.2, -31.32) * mm});
            skPoint(sketch, "E409", {"position": v(10.93, -40) * mm});
            skPoint(sketch, "E410", {"position": v(14.68, -38.32) * mm});
            skPoint(sketch, "E411", {"position": v(14.22, -42.94) * mm});
            skPoint(sketch, "E412", {"position": v(13.24, -46.53) * mm});
            skPoint(sketch, "E413", {"position": v(11.68, -49.94) * mm});
            skPoint(sketch, "E414", {"position": v(10.23, -52.88) * mm});
            skPoint(sketch, "E415", {"position": v(8.33, -55.72) * mm});
            skPoint(sketch, "E416", {"position": v(5.2, -58.84) * mm});
            skPoint(sketch, "E417", {"position": v(7.69, -54.16) * mm});
            skPoint(sketch, "E418", {"position": v(9.08, -50.75) * mm});
            skPoint(sketch, "E419", {"position": v(10.35, -46.7) * mm});
            skPoint(sketch, "E420", {"position": v(10.81, -43.11) * mm});
            skPoint(sketch, "E421", {"position": v(9.42, -41.67) * mm});
            skPoint(sketch, "E422", {"position": v(9.2, -44.96) * mm});
            skPoint(sketch, "E423", {"position": v(9.14, -48.09) * mm});
            skPoint(sketch, "E424", {"position": v(8.56, -49.94) * mm});
            skPoint(sketch, "E425", {"position": v(7.11, -51.27) * mm});
            skPoint(sketch, "E426", {"position": v(5.2, -47.74) * mm});
            skPoint(sketch, "E427", {"position": v(6.24, -45.43) * mm});
            skPoint(sketch, "E428", {"position": v(7.46, -42.88) * mm});
            skPoint(sketch, "E429", {"position": v(35.38, -28.08) * mm});
            skPoint(sketch, "E430", {"position": v(38.33, -25.6) * mm});
            skPoint(sketch, "E431", {"position": v(37.87, -28.9) * mm});
            skPoint(sketch, "E432", {"position": v(35.55, -32.25) * mm});
            skPoint(sketch, "E433", {"position": v(33.18, -34.15) * mm});
            skPoint(sketch, "E434", {"position": v(37.29, -32.82) * mm});
            skPoint(sketch, "E435", {"position": v(40, -30.69) * mm});
            skPoint(sketch, "E436", {"position": v(42.32, -28.32) * mm});
            skPoint(sketch, "E437", {"position": v(44.28, -25.54) * mm});
            skPoint(sketch, "E438", {"position": v(46.65, -21.15) * mm});
            skPoint(sketch, "E439", {"position": v(46.25, -16.7) * mm});
            skPoint(sketch, "E440", {"position": v(45.27, -11.72) * mm});
            skPoint(sketch, "E441", {"position": v(43.53, -6.64) * mm});
            skPoint(sketch, "E442", {"position": v(41.74, -3.4) * mm});
            skPoint(sketch, "E443", {"position": v(39.48, 0) * mm});
            skPoint(sketch, "E444", {"position": v(36.88, 2.55) * mm});
            skPoint(sketch, "E445", {"position": v(33.59, 5.56) * mm});
            skPoint(sketch, "E446", {"position": v(29.31, 8.4) * mm});
            skPoint(sketch, "E447", {"position": v(25.32, 10.42) * mm});
            skPoint(sketch, "E448", {"position": v(20.87, 12.27) * mm});
            skPoint(sketch, "E449", {"position": v(15.5, 13.94) * mm});
            skPoint(sketch, "E450", {"position": v(18.44, 11.8) * mm});
            skPoint(sketch, "E451", {"position": v(21.91, 9.32) * mm});
            skPoint(sketch, "E452", {"position": v(27.06, 5.9) * mm});
            skPoint(sketch, "E453", {"position": v(30.87, 2.79) * mm});
            skPoint(sketch, "E454", {"position": v(33.82, -0.8) * mm});
            skPoint(sketch, "E455", {"position": v(35.73, -4.44) * mm});
            skPoint(sketch, "E456", {"position": v(36.54, -8.08) * mm});
            skPoint(sketch, "E457", {"position": v(34.8, -8.55) * mm});
            skPoint(sketch, "E458", {"position": v(32.72, -7.5) * mm});
            skPoint(sketch, "E459", {"position": v(31.22, -5.94) * mm});
            skPoint(sketch, "E460", {"position": v(29.77, -3.86) * mm});
            skPoint(sketch, "E461", {"position": v(28.85, -1.09) * mm});
            skPoint(sketch, "E462", {"position": v(26.13, 1.63) * mm});
            skPoint(sketch, "E463", {"position": v(22.72, 4.29) * mm});
            skPoint(sketch, "E464", {"position": v(18.21, 7.24) * mm});
            skPoint(sketch, "E465", {"position": v(14.28, 10.3) * mm});
            skPoint(sketch, "E466", {"position": v(10.7, 14.58) * mm});
            skPoint(sketch, "E467", {"position": v(11.62, 16.43) * mm});
            skPoint(sketch, "E468", {"position": v(13.07, 17.64) * mm});
            skPoint(sketch, "E469", {"position": v(14.86, 18.22) * mm});
            skPoint(sketch, "E470", {"position": v(17.4, 18.5) * mm});
            skPoint(sketch, "E471", {"position": v(22.09, 18.68) * mm});
            skPoint(sketch, "E472", {"position": v(20.7, 19.9) * mm});
            skPoint(sketch, "E473", {"position": v(17.63, 20.94) * mm});
            skPoint(sketch, "E474", {"position": v(14.68, 21.57) * mm});
            skPoint(sketch, "E475", {"position": v(11.8, 21.57) * mm});
            skPoint(sketch, "E476", {"position": v(9.3, 21.4) * mm});
            skPoint(sketch, "E477", {"position": v(7, 20.36) * mm});
            skPoint(sketch, "E478", {"position": v(5.38, 18.8) * mm});
            skPoint(sketch, "E479", {"position": v(2.43, 16.2) * mm});
            skPoint(sketch, "E480", {"position": v(2.66, 18.34) * mm});
            skPoint(sketch, "E481", {"position": v(3.82, 20.3) * mm});
            skPoint(sketch, "E482", {"position": v(5.38, 21.63) * mm});
            skPoint(sketch, "E483", {"position": v(7.11, 22.61) * mm});
            skPoint(sketch, "E484", {"position": v(9.54, 23.37) * mm});
            skPoint(sketch, "E485", {"position": v(11.1, 23.77) * mm});
            skPoint(sketch, "E486", {"position": v(11.1, 26.72) * mm});
            skPoint(sketch, "E487", {"position": v(19.83, 14.7) * mm});
            skPoint(sketch, "E488", {"position": v(21.1, 15.73) * mm});
            skPoint(sketch, "E489", {"position": v(24.86, 16.14) * mm});
            skPoint(sketch, "E490", {"position": v(24.57, 17.64) * mm});
            skPoint(sketch, "E491", {"position": v(23.59, 19.43) * mm});
            skPoint(sketch, "E492", {"position": v(22.14, 20.65) * mm});
            skPoint(sketch, "E493", {"position": v(20.4, 21.4) * mm});
            skPoint(sketch, "E494", {"position": v(18.44, 22.32) * mm});
            skPoint(sketch, "E495", {"position": v(16.19, 23.13) * mm});
            skPoint(sketch, "E496", {"position": v(14.22, 24.3) * mm});
            skPoint(sketch, "E497", {"position": v(14.28, 26.54) * mm});
            skPoint(sketch, "E498", {"position": v(14.92, 28.74) * mm});
            skPoint(sketch, "E499", {"position": v(22.55, 13.65) * mm});
            skPoint(sketch, "E500", {"position": v(25.26, 12.27) * mm});
            skPoint(sketch, "E501", {"position": v(28.56, 10.59) * mm});
            skPoint(sketch, "E502", {"position": v(31.05, 9.09) * mm});
            skPoint(sketch, "E503", {"position": v(33.13, 7.35) * mm});
            skPoint(sketch, "E504", {"position": v(35.5, 5.44) * mm});
            skPoint(sketch, "E505", {"position": v(37.87, 3.3) * mm});
            skPoint(sketch, "E506", {"position": v(39.54, 1.63) * mm});
            skPoint(sketch, "E507", {"position": v(41.8, 4.64) * mm});
            skPoint(sketch, "E508", {"position": v(39.43, 8.28) * mm});
            skPoint(sketch, "E509", {"position": v(37.7, 10.88) * mm});
            skPoint(sketch, "E510", {"position": v(36.02, 12.9) * mm});
            skPoint(sketch, "E511", {"position": v(34.63, 15.68) * mm});
            skPoint(sketch, "E512", {"position": v(37.46, 15.27) * mm});
            skPoint(sketch, "E513", {"position": v(38.97, 14.17) * mm});
            skPoint(sketch, "E514", {"position": v(40.59, 12.73) * mm});
            skPoint(sketch, "E515", {"position": v(40.24, 14.58) * mm});
            skPoint(sketch, "E516", {"position": v(39.49, 16.31) * mm});
            skPoint(sketch, "E517", {"position": v(37.52, 17.99) * mm});
            skPoint(sketch, "E518", {"position": v(35.38, 19.15) * mm});
            skPoint(sketch, "E519", {"position": v(33.7, 20.13) * mm});
            skPoint(sketch, "E520", {"position": v(32.09, 21.17) * mm});
            skPoint(sketch, "E521", {"position": v(30.47, 23.2) * mm});
            skPoint(sketch, "E522", {"position": v(31.62, 24.12) * mm});
            skPoint(sketch, "E523", {"position": v(33.19, 24.4) * mm});
            skPoint(sketch, "E524", {"position": v(34.57, 24.4) * mm});
            skPoint(sketch, "E525", {"position": v(35.96, 25.1) * mm});
            skPoint(sketch, "E526", {"position": v(36.42, 25.85) * mm});
            skPoint(sketch, "E527", {"position": v(35.27, 25.9) * mm});
            skPoint(sketch, "E528", {"position": v(30.47, 27.35) * mm});
            skPoint(sketch, "E529", {"position": v(32.55, 26.49) * mm});
            skPoint(sketch, "E530", {"position": v(27.17, 28.68) * mm});
            skPoint(sketch, "E531", {"position": v(24.51, 29.78) * mm});
            skPoint(sketch, "E532", {"position": v(21.91, 30.77) * mm});
            skPoint(sketch, "E533", {"position": v(18.04, 31.34) * mm});
            skPoint(sketch, "E534", {"position": v(16.01, 30.42) * mm});
            skPoint(sketch, "E535", {"position": v(12.26, 29.26) * mm});
            skPoint(sketch, "E536", {"position": v(14.22, 31.34) * mm});
            skPoint(sketch, "E537", {"position": v(16.7, 32.5) * mm});
            skPoint(sketch, "E538", {"position": v(19.66, 33.37) * mm});
            skPoint(sketch, "E539", {"position": v(22.2, 33.42) * mm});
            skPoint(sketch, "E540", {"position": v(25.15, 33.3) * mm});
            skPoint(sketch, "E541", {"position": v(30.06, 33.02) * mm});
            skPoint(sketch, "E542", {"position": v(27.29, 34.75) * mm});
            skPoint(sketch, "E543", {"position": v(25.15, 35.62) * mm});
            skPoint(sketch, "E544", {"position": v(22.14, 36.66) * mm});
            skPoint(sketch, "E545", {"position": v(18.62, 37.64) * mm});
            skPoint(sketch, "E546", {"position": v(15.44, 38.22) * mm});
            skPoint(sketch, "E547", {"position": v(12.08, 38.51) * mm});
            skPoint(sketch, "E548", {"position": v(9.25, 38.57) * mm});
            skPoint(sketch, "E549", {"position": v(5.78, 38.22) * mm});
            skPoint(sketch, "E550", {"position": v(6.76, 39.55) * mm});
            skPoint(sketch, "E551", {"position": v(7.69, 39.96) * mm});
            skPoint(sketch, "E552", {"position": v(9.3, 40.42) * mm});
            skPoint(sketch, "E553", {"position": v(12.37, 41.06) * mm});
            skPoint(sketch, "E554", {"position": v(9.83, 42.44) * mm});
            skPoint(sketch, "E555", {"position": v(6.6, 43.43) * mm});
            skPoint(sketch, "E556", {"position": v(2.95, 44.18) * mm});
            skPoint(sketch, "E557", {"position": v(-1.21, 44.7) * mm});
            skPoint(sketch, "E558", {"position": v(-5.2, 44.81) * mm});
            skPoint(sketch, "E559", {"position": v(-8.44, 44.58) * mm});
            skPoint(sketch, "E560", {"position": v(-11.9, 43.83) * mm});
            skPoint(sketch, "E561", {"position": v(-15.44, 42.96) * mm});
            skPoint(sketch, "E562", {"position": v(-17.92, 41.58) * mm});
            skPoint(sketch, "E563", {"position": v(-20.75, 39.55) * mm});
            skPoint(sketch, "E564", {"position": v(-22.49, 36.9) * mm});
            skPoint(sketch, "E565", {"position": v(-23.3, 34.12) * mm});
            skPoint(sketch, "E566", {"position": v(-23.36, 31.8) * mm});
            skPoint(sketch, "E567", {"position": v(-24.69, 32.5) * mm});
            skPoint(sketch, "E568", {"position": v(-25.15, 33.71) * mm});
            skPoint(sketch, "E569", {"position": v(-25.96, 32.56) * mm});
            skPoint(sketch, "E570", {"position": v(-25.26, 30.3) * mm});
            skPoint(sketch, "E571", {"position": v(-23.82, 29.32) * mm});
            skPoint(sketch, "E572", {"position": v(-21.5, 28.8) * mm});
            skPoint(sketch, "E573", {"position": v(-19.37, 29.5) * mm});
            skPoint(sketch, "E574", {"position": v(-19.95, 31.63) * mm});
            skPoint(sketch, "E575", {"position": v(-19.43, 33.94) * mm});
            skPoint(sketch, "E576", {"position": v(-17.98, 36.14) * mm});
            skPoint(sketch, "E577", {"position": v(-16.42, 37.53) * mm});
            skPoint(sketch, "E578", {"position": v(-14.28, 38.74) * mm});
            skPoint(sketch, "E579", {"position": v(-11.85, 39.44) * mm});
            skPoint(sketch, "E580", {"position": v(-9.6, 39.2) * mm});
            skPoint(sketch, "E581", {"position": v(-7.52, 38.57) * mm});
            skPoint(sketch, "E582", {"position": v(-10.23, 37.82) * mm});
            skPoint(sketch, "E583", {"position": v(-12.37, 37.12) * mm});
            skPoint(sketch, "E584", {"position": v(-14.63, 36.14) * mm});
            skPoint(sketch, "E585", {"position": v(-16.13, 34.58) * mm});
            skPoint(sketch, "E586", {"position": v(-16.53, 32.96) * mm});
            skPoint(sketch, "E587", {"position": v(-16.3, 31.4) * mm});
            skPoint(sketch, "E588", {"position": v(-15.15, 31.29) * mm});
            skPoint(sketch, "E589", {"position": v(-13.7, 32.44) * mm});
            skPoint(sketch, "E590", {"position": v(-11.56, 33.94) * mm});
            skPoint(sketch, "E591", {"position": v(-11.56, 31.4) * mm});
            skPoint(sketch, "E592", {"position": v(-11.62, 28.63) * mm});
            skPoint(sketch, "E593", {"position": v(-10.87, 28.16) * mm});
            skPoint(sketch, "E594", {"position": v(-9.42, 27.12) * mm});
            skPoint(sketch, "E595", {"position": v(-8.04, 26.9) * mm});
            skPoint(sketch, "E596", {"position": v(-7.4, 28.68) * mm});
            skPoint(sketch, "E597", {"position": v(-6.6, 30.19) * mm});
            skPoint(sketch, "E598", {"position": v(-5.6, 31.92) * mm});
            skPoint(sketch, "E599", {"position": v(-3.99, 33.3) * mm});
            skPoint(sketch, "E600", {"position": v(-2.43, 34.18) * mm});
            skPoint(sketch, "E601", {"position": v(0, 34.46) * mm});
            skPoint(sketch, "E602", {"position": v(2.14, 33.66) * mm});
            skPoint(sketch, "E603", {"position": v(4.05, 31.4) * mm});
            skPoint(sketch, "E604", {"position": v(4.86, 28.97) * mm});
            skPoint(sketch, "E605", {"position": v(4.68, 26.43) * mm});
            skPoint(sketch, "E606", {"position": v(3.35, 24) * mm});
            skPoint(sketch, "E607", {"position": v(1.21, 22.79) * mm});
            skPoint(sketch, "E608", {"position": v(-1.1, 22.61) * mm});
            skPoint(sketch, "E609", {"position": v(-1.73, 24.46) * mm});
            skPoint(sketch, "E610", {"position": v(-1.56, 25.68) * mm});
            skPoint(sketch, "E611", {"position": v(-1.04, 26.95) * mm});
            skPoint(sketch, "E612", {"position": v(-0.06, 27.35) * mm});
            skPoint(sketch, "E613", {"position": v(-0.17, 28.28) * mm});
            skPoint(sketch, "E614", {"position": v(-1.16, 28.68) * mm});
            skPoint(sketch, "E615", {"position": v(-1.5, 28.92) * mm});
            skPoint(sketch, "E616", {"position": v(-1.62, 29.5) * mm});
            skPoint(sketch, "E617", {"position": v(-0.87, 29.96) * mm});
            skPoint(sketch, "E618", {"position": v(0.23, 30.19) * mm});
            skPoint(sketch, "E619", {"position": v(1.39, 30.19) * mm});
            skPoint(sketch, "E620", {"position": v(2.31, 30.42) * mm});
            skPoint(sketch, "E621", {"position": v(1.45, 31.11) * mm});
            skFitSpline(sketch, "E622", {"points": [v(18.85, -49.53) * mm, v(21.74, -45.89) * mm, v(24.97, -41.32) * mm, v(28.39, -36.24) * mm, v(32.2, -31.32) * mm, v(35.38, -28.08) * mm, v(38.33, -25.6) * mm, v(37.87, -28.9) * mm, v(35.55, -32.25) * mm, v(33.18, -34.15) * mm, v(37.29, -32.82) * mm, v(40, -30.69) * mm, v(42.32, -28.32) * mm, v(44.28, -25.54) * mm, v(46.65, -21.15) * mm, v(46.25, -16.7) * mm, v(45.27, -11.72) * mm, v(43.53, -6.64) * mm, v(41.74, -3.4) * mm, v(39.48, 0) * mm, v(36.88, 2.55) * mm, v(33.59, 5.56) * mm, v(29.31, 8.4) * mm, v(25.32, 10.42) * mm, v(20.87, 12.27) * mm, v(15.5, 13.94) * mm, v(18.44, 11.8) * mm, v(21.91, 9.32) * mm, v(27.06, 5.9) * mm, v(30.87, 2.79) * mm, v(33.82, -0.8) * mm, v(35.73, -4.44) * mm, v(36.54, -8.08) * mm, v(34.8, -8.55) * mm, v(32.72, -7.5) * mm, v(31.22, -5.94) * mm, v(29.77, -3.86) * mm, v(28.85, -1.09) * mm, v(26.13, 1.63) * mm, v(22.72, 4.29) * mm, v(18.21, 7.24) * mm, v(14.28, 10.3) * mm, v(10.7, 14.58) * mm, v(11.62, 16.43) * mm, v(13.07, 17.64) * mm, v(14.86, 18.22) * mm, v(17.4, 18.5) * mm, v(22.09, 18.68) * mm, v(20.7, 19.9) * mm, v(17.63, 20.94) * mm, v(14.68, 21.57) * mm, v(11.8, 21.57) * mm, v(9.3, 21.4) * mm, v(7, 20.36) * mm, v(5.38, 18.8) * mm, v(4.45, 15.9) * mm, v(6.48, 12.61) * mm, v(8.96, 9.43) * mm, v(11.56, 6.89) * mm, v(14.63, 3.3) * mm, v(17.8, 0) * mm, v(19.89, -3.52) * mm, v(22.49, -8.66) * mm, v(23.76, -13.98) * mm, v(24.45, -18.66) * mm, v(24.45, -23.4) * mm, v(24, -28.26) * mm, v(23.3, -33.35) * mm, v(22.32, -37.68) * mm, v(21.27, -42.02) * mm, v(18.85, -49.53) * mm]});
            skFitSpline(sketch, "E623", {"points": [v(10.93, -40) * mm, v(14.68, -38.32) * mm, v(14.22, -42.94) * mm], "startDerivative": vector(9.85, 6.47) * mm, "endDerivative": vector(-3.13, -12.18) * mm});
            skFitSpline(sketch, "E624", {"points": [v(10.93, -40) * mm, v(10.81, -43.11) * mm, v(10.35, -46.7) * mm, v(9.08, -51.35) * mm, v(7.69, -54.16) * mm, v(5.2, -58.84) * mm, v(8.33, -55.72) * mm, v(10.23, -52.88) * mm, v(11.68, -49.94) * mm, v(13.24, -46.53) * mm, v(14.22, -42.94) * mm], "startDerivative": vector(-0.82, -34.57) * mm, "endDerivative": vector(8.43, 36.81) * mm});
            skFitSpline(sketch, "E625", {"points": [v(-1.04, 17.67) * mm, v(-0.61, 15.53) * mm, v(0, 13.2) * mm, v(1.47, 10.87) * mm, v(3.24, 8.55) * mm, v(4.9, 6.9) * mm, v(7.53, 5.48) * mm, v(10.96, 4.5) * mm, v(9.18, 2.18) * mm, v(7.9, 0) * mm, v(7.04, -2.79) * mm, v(6.73, -5.48) * mm, v(7.04, -8.05) * mm, v(7.84, -10.69) * mm, v(8.94, -12.95) * mm, v(11.39, -14.91) * mm, v(13.04, -15.77) * mm, v(11.08, -16.26) * mm, v(8.7, -17.06) * mm, v(6.3, -18.28) * mm, v(3.61, -20.12) * mm, v(1.47, -22.38) * mm, v(0, -24.59) * mm, v(-1.41, -26.8) * mm, v(-2.33, -29.49) * mm, v(-3.06, -32.37) * mm, v(-3.3, -35) * mm, v(-3, -37.94) * mm, v(-2.2, -42.17) * mm, v(-5.83, -39.06) * mm, v(-7.78, -35.03) * mm, v(-9.08, -30.62) * mm, v(-8.69, -25.82) * mm, v(-8.3, -21.4) * mm, v(-6.87, -17.13) * mm, v(-5.31, -13.1) * mm, v(-2.98, -8.3) * mm, v(0, -4.15) * mm, v(1.57, -1.42) * mm, v(0.92, 1.82) * mm, v(0, 4.01) * mm, v(-1.04, 5.97) * mm, v(-2.51, 8) * mm, v(-3.86, 9.7) * mm, v(-4.72, 11.8) * mm, v(-4.17, 14.3) * mm, v(-2.82, 16.26) * mm, v(-1.04, 17.67) * mm]});
            skLineSegment(sketch, "E626", {"start": v(5.2, -47.74) * mm, "end": v(7.11, -51.27) * mm});
            skFitSpline(sketch, "E627", {"points": [v(7.11, -51.27) * mm, v(8.56, -49.94) * mm, v(9.14, -48.09) * mm, v(9.2, -44.96) * mm, v(9.42, -41.67) * mm, v(7.46, -42.88) * mm, v(6.24, -45.43) * mm, v(5.2, -47.74) * mm], "startDerivative": vector(12.98, 9.64) * mm, "endDerivative": vector(-7.85, -15.97) * mm});
            skFitSpline(sketch, "E628", {"points": [v(0.5, -50.24) * mm, v(0.46, -47.87) * mm, v(0.86, -45) * mm, v(2.2, -41.46) * mm, v(3.77, -38.8) * mm, v(5.56, -36.47) * mm, v(7.52, -34.07) * mm, v(9.16, -32.17) * mm, v(10.76, -30.28) * mm, v(11.93, -28.6) * mm, v(12.44, -27.59) * mm, v(11.06, -27.62) * mm, v(9.16, -28.13) * mm, v(7.81, -28.9) * mm, v(6.69, -30.03) * mm, v(5.08, -31.63) * mm, v(4.03, -33.41) * mm, v(3, -35.27) * mm, v(1.91, -37.35) * mm, v(0.49, -39.47) * mm, v(0, -36.72) * mm, v(0, -32.86) * mm, v(0.31, -30.57) * mm, v(0.97, -27.99) * mm, v(2.13, -25.55) * mm, v(3.88, -23.5) * mm, v(7.05, -23.07) * mm, v(9.42, -21.87) * mm, v(11.5, -20.3) * mm, v(12.84, -18.48) * mm, v(13.9, -15.9) * mm, v(14.37, -14.04) * mm, v(14.44, -11.85) * mm, v(13.93, -9.7) * mm, v(12.8, -7.85) * mm, v(11.67, -6.46) * mm, v(9.7, -5.04) * mm, v(10.7, -4.68) * mm, v(12.18, -5.15) * mm, v(13.64, -6.03) * mm, v(15.28, -7.27) * mm, v(17.06, -9.34) * mm, v(18.08, -11.09) * mm, v(19, -13.16) * mm, v(19.69, -15.1) * mm, v(20.34, -17.72) * mm, v(20.92, -20.56) * mm, v(21.03, -23.22) * mm, v(20.85, -26.02) * mm, v(20.6, -28.06) * mm, v(20.2, -30.1) * mm, v(19.36, -32.54) * mm, v(18.3, -34.72) * mm, v(17.61, -35.74) * mm, v(14.95, -36.36) * mm, v(12.73, -37.38) * mm, v(10.25, -39.06) * mm, v(8.83, -40.48) * mm, v(6.83, -42.52) * mm, v(5.3, -44.41) * mm, v(3.92, -46.16) * mm, v(2.6, -47.69) * mm, v(1.48, -49.25) * mm, v(0.5, -50.24) * mm]});
            skFitSpline(sketch, "E629", {"points": [v(-4.64, -48.96) * mm, v(-5.62, -47.87) * mm, v(-7.37, -45.92) * mm, v(-8.91, -43.24) * mm, v(-10.4, -39.9) * mm, v(-11.33, -36.34) * mm, v(-11.9, -33.04) * mm, v(-12.2, -29.9) * mm, v(-11.9, -26.7) * mm, v(-11.9, -23.46) * mm, v(-11.64, -21.35) * mm, v(-10.97, -18.62) * mm, v(-10.25, -16.3) * mm, v(-9.22, -13.83) * mm, v(-8.09, -11.46) * mm, v(-6.08, -8.78) * mm, v(-3.3, -6.36) * mm, v(-5.82, -7.7) * mm, v(-7.99, -9.15) * mm, v(-9.94, -10.9) * mm, v(-11.64, -12.34) * mm, v(-12.88, -13.68) * mm, v(-14.73, -15.63) * mm, v(-16.23, -17.54) * mm, v(-17.51, -18.93) * mm, v(-18.65, -20.01) * mm, v(-19.68, -21.6) * mm, v(-21.02, -23.41) * mm, v(-22.77, -24.5) * mm, v(-24.42, -24.5) * mm, v(-24.88, -23.36) * mm, v(-24.67, -20.63) * mm, v(-23.85, -18.47) * mm, v(-22.25, -16.36) * mm, v(-19.93, -14.7) * mm, v(-17.98, -13.42) * mm, v(-16.07, -12.29) * mm, v(-14.06, -11.2) * mm, v(-12.1, -9.97) * mm, v(-9.22, -8.32) * mm, v(-6.9, -6.88) * mm, v(-5.36, -5.6) * mm, v(-3.4, -3.79) * mm, v(-2.17, -2.14) * mm, v(-1.3, -0.39) * mm, v(-1.3, 1.93) * mm, v(-1.14, 3.73) * mm, v(-1.65, 5.17) * mm, v(-2.42, 6.46) * mm, v(-3.5, 7.85) * mm], "startDerivative": vector(-56.1, 63.93) * mm, "endDerivative": vector(-65.63, 80.22) * mm});
            skFitSpline(sketch, "E630", {"points": [v(-42.44, -10.84) * mm, v(-41.62, -11.51) * mm, v(-40.54, -11.26) * mm, v(-39.97, -11.41) * mm, v(-38.63, -12.18) * mm, v(-36.83, -13.06) * mm, v(-35.33, -12.34) * mm, v(-34.1, -11.62) * mm, v(-31.93, -10.74) * mm, v(-29.93, -10.07) * mm, v(-27.3, -9.92) * mm, v(-25.96, -10.28) * mm, v(-24.83, -10.43) * mm, v(-27.2, -12.54) * mm, v(-29.2, -15.63) * mm, v(-30.5, -18.83) * mm, v(-31.16, -21.71) * mm, v(-31.32, -25.57) * mm, v(-30.96, -28.61) * mm, v(-29.82, -32.37) * mm, v(-28.43, -34.69) * mm, v(-26.42, -36.39) * mm, v(-23.39, -37.52) * mm, v(-24.16, -36.75) * mm, v(-25.09, -35.05) * mm, v(-25.24, -33.14) * mm, v(-24.36, -31.7) * mm, v(-20.66, -34.12) * mm, v(-18.6, -36.6) * mm, v(-16.38, -38.5) * mm, v(-13.34, -41.33) * mm, v(-10.51, -44.11) * mm, v(-7.52, -47.1) * mm, v(-4.64, -48.96) * mm, v(-5.62, -47.87) * mm], "startDerivative": vector(37.52, -48.5) * mm, "endDerivative": vector(-69.72, 67.29) * mm});
            skLineSegment(sketch, "E631", {"start": v(-42.44, -6.31) * mm, "end": v(-42.44, -10.84) * mm});
            skLineSegment(sketch, "E632", {"start": v(-42.2, -11.16) * mm, "end": v(-41.62, -11.51) * mm});
            skLineSegment(sketch, "E633", {"start": v(-42.44, -6.31) * mm, "end": v(-41.77, -5.54) * mm});
            skFitSpline(sketch, "E634", {"points": [v(-25.15, 33.71) * mm, v(-24.69, 32.5) * mm, v(-23.36, 31.8) * mm, v(-23.3, 34.12) * mm, v(-22.49, 36.9) * mm, v(-20.75, 39.55) * mm, v(-17.92, 41.58) * mm, v(-15.44, 42.96) * mm, v(-11.9, 43.83) * mm, v(-8.44, 44.58) * mm, v(-5.2, 44.81) * mm, v(-1.21, 44.7) * mm, v(2.95, 44.18) * mm, v(6.6, 43.43) * mm, v(9.83, 42.44) * mm, v(12.37, 41.06) * mm, v(9.3, 40.42) * mm, v(7.69, 39.96) * mm, v(6.76, 39.55) * mm, v(5.78, 38.22) * mm, v(9.25, 38.57) * mm, v(12.08, 38.51) * mm, v(15.44, 38.22) * mm, v(18.62, 37.64) * mm, v(22.14, 36.66) * mm, v(25.15, 35.62) * mm, v(27.29, 34.75) * mm, v(30.06, 33.02) * mm, v(25.15, 33.3) * mm, v(22.2, 33.42) * mm, v(19.66, 33.37) * mm, v(16.7, 32.5) * mm, v(14.22, 31.34) * mm, v(12.26, 29.26) * mm, v(11.1, 26.72) * mm, v(11.1, 23.77) * mm, v(9.54, 23.37) * mm, v(7.11, 22.61) * mm, v(5.38, 21.63) * mm, v(3.82, 20.3) * mm, v(2.66, 18.34) * mm, v(2.43, 16.2) * mm, v(-1.1, 22.61) * mm, v(1.21, 22.79) * mm, v(3.35, 24) * mm, v(4.68, 26.43) * mm, v(4.86, 28.97) * mm, v(4.05, 31.4) * mm, v(2.14, 33.66) * mm, v(0, 34.46) * mm, v(-2.43, 34.18) * mm, v(-3.99, 33.3) * mm, v(-5.6, 31.92) * mm, v(-6.6, 30.19) * mm, v(-7.4, 28.68) * mm, v(-8.04, 26.9) * mm, v(-9.42, 27.12) * mm, v(-10.87, 28.16) * mm, v(-11.62, 28.63) * mm, v(-11.56, 31.4) * mm, v(-11.56, 33.94) * mm, v(-13.7, 32.44) * mm, v(-15.15, 31.29) * mm, v(-16.3, 31.4) * mm, v(-16.53, 32.96) * mm, v(-16.13, 34.58) * mm, v(-14.63, 36.14) * mm, v(-12.37, 37.12) * mm, v(-10.23, 37.82) * mm, v(-7.52, 38.57) * mm, v(-9.6, 39.2) * mm, v(-11.85, 39.44) * mm, v(-14.28, 38.74) * mm, v(-16.42, 37.53) * mm, v(-17.98, 36.14) * mm, v(-19.43, 33.94) * mm, v(-19.95, 31.63) * mm, v(-19.37, 29.5) * mm, v(-21.5, 28.8) * mm, v(-23.82, 29.32) * mm, v(-25.26, 30.3) * mm, v(-25.96, 32.56) * mm, v(-25.15, 33.71) * mm]});
            skPoint(sketch, "E635", {"position": v(0, 31.38) * mm});
            skPoint(sketch, "E636", {"position": v(-1.14, 31.35) * mm});
            skPoint(sketch, "E637", {"position": v(-2.86, 30.96) * mm});
            skPoint(sketch, "E638", {"position": v(-4.1, 30.35) * mm});
            skPoint(sketch, "E639", {"position": v(-5, 29.34) * mm});
            skPoint(sketch, "E640", {"position": v(-5.46, 28.27) * mm});
            skPoint(sketch, "E641", {"position": v(-5.62, 26.84) * mm});
            skPoint(sketch, "E642", {"position": v(-4.32, 26.52) * mm});
            skFitSpline(sketch, "E643", {"points": [v(-5.62, 26.84) * mm, v(-4.32, 26.52) * mm, v(-1.73, 24.46) * mm, v(-1.56, 25.68) * mm, v(-1.04, 26.95) * mm, v(-0.06, 27.35) * mm, v(-0.17, 28.28) * mm, v(-1.16, 28.68) * mm, v(-1.5, 28.92) * mm, v(-1.62, 29.5) * mm, v(-0.87, 29.96) * mm, v(0.23, 30.19) * mm, v(1.39, 30.19) * mm, v(2.31, 30.42) * mm, v(1.45, 31.11) * mm, v(0, 31.38) * mm, v(-1.14, 31.35) * mm, v(-2.86, 30.96) * mm, v(-4.1, 30.35) * mm, v(-5, 29.34) * mm, v(-5.46, 28.27) * mm, v(-5.62, 26.84) * mm]});
            skFitSpline(sketch, "E644", {"points": [v(14.28, 26.54) * mm, v(14.92, 28.74) * mm, v(16.01, 30.42) * mm, v(18.04, 31.34) * mm, v(21.91, 30.77) * mm, v(24.51, 29.78) * mm, v(27.17, 28.68) * mm, v(30.47, 27.35) * mm, v(32.55, 26.49) * mm, v(35.27, 25.9) * mm, v(36.42, 25.85) * mm, v(35.96, 25.1) * mm, v(34.57, 24.4) * mm, v(33.19, 24.4) * mm, v(31.62, 24.12) * mm, v(30.47, 23.2) * mm, v(32.09, 21.17) * mm, v(33.7, 20.13) * mm, v(35.38, 19.15) * mm, v(37.52, 17.99) * mm, v(39.49, 16.31) * mm, v(40.24, 14.58) * mm, v(40.59, 12.73) * mm, v(38.97, 14.17) * mm, v(37.46, 15.27) * mm, v(34.63, 15.68) * mm, v(36.02, 12.9) * mm, v(37.7, 10.88) * mm, v(39.43, 8.28) * mm, v(41.8, 4.64) * mm], "startDerivative": vector(15.43, 65.7) * mm, "endDerivative": vector(51.53, -78.5) * mm});
            skPoint(sketch, "E645", {"position": v(43.15, 0.85) * mm});
            skPoint(sketch, "E646", {"position": v(43.56, -2.35) * mm});
            skFitSpline(sketch, "E647", {"points": [v(41.8, 4.64) * mm, v(43.15, 0.85) * mm, v(43.56, -2.35) * mm, v(39.54, 1.63) * mm, v(37.87, 3.3) * mm, v(35.5, 5.44) * mm, v(33.13, 7.35) * mm, v(31.05, 9.09) * mm, v(28.56, 10.59) * mm, v(25.26, 12.27) * mm, v(22.55, 13.65) * mm, v(19.83, 14.7) * mm, v(21.1, 15.73) * mm, v(24.86, 16.14) * mm, v(24.57, 17.64) * mm, v(23.59, 19.43) * mm, v(22.14, 20.65) * mm, v(20.4, 21.4) * mm, v(18.44, 22.32) * mm, v(16.19, 23.13) * mm, v(14.22, 24.3) * mm, v(14.28, 26.54) * mm, v(14.46, 27.3) * mm], "startDerivative": vector(23.23, -59.57) * mm, "endDerivative": vector(5.85, 24.6) * mm});
            skSolve(sketch);
        }
        {
            var Q0;
            Q0=makeQuery(id+"F1.imprint","IMPRINT",FACE,{"disambiguationData":[TD([[makeQuery(id+"F1.imprint","IMPRINT",EDGE,{"derivedFrom":sQuery(id+"F1.wireOp",EDGE,"E634")}),-1.0]])]});
            extrude(context, id + "F2", {"entities" : qUnion([Q0]), "depth" : 60 * mm});
        }
        {
            var Q0;
            Q0=makeQuery(id+"F1.imprint","IMPRINT",FACE,{"disambiguationData":[TD([[makeQuery(id+"F1.imprint","IMPRINT",EDGE,{"derivedFrom":sQuery(id+"F1.wireOp",EDGE,"E32")}),-1.0]])]});
            extrude(context, id + "F3", {"entities" : qUnion([Q0]), "depth" : 60 * mm});
        }
        {
            var Q0;
            Q0=makeQuery(id+"F1.imprint","IMPRINT",FACE,{"disambiguationData":[TD([[makeQuery(id+"F1.imprint","IMPRINT",EDGE,{"derivedFrom":sQuery(id+"F1.wireOp",EDGE,"E275")}),-1.0]])]});
            extrude(context, id + "F4", {"entities" : qUnion([Q0]), "depth" : 60 * mm});
        }
        {
            var Q0;
            Q0=makeQuery(id+"F1.imprint","IMPRINT",FACE,{"disambiguationData":[TD([[makeQuery(id+"F1.imprint","IMPRINT",EDGE,{"derivedFrom":sQuery(id+"F1.wireOp",EDGE,"E625")}),-1.0]])]});
            extrude(context, id + "F5", {"entities" : qUnion([Q0]), "depth" : 60 * mm});
        }
        {
            var Q0;
            Q0=makeQuery(id+"F1.imprint","IMPRINT",FACE,{"disambiguationData":[TD([[makeQuery(id+"F1.imprint","IMPRINT",EDGE,{"derivedFrom":sQuery(id+"F1.wireOp",EDGE,"E628")}),-1.0]])]});
            extrude(context, id + "F6", {"entities" : qUnion([Q0]), "depth" : 60 * mm});
        }
        {
            var Q0;
            Q0=makeQuery(id+"F1.imprint","IMPRINT",FACE,{"disambiguationData":[TD([[makeQuery(id+"F1.imprint","IMPRINT",EDGE,{"derivedFrom":sQuery(id+"F1.wireOp",EDGE,"E622")}),1.0]])]});
            extrude(context, id + "F7", {"entities" : qUnion([Q0]), "depth" : 60 * mm});
        }
        {
            var Q0;
            Q0=makeQuery(id+"F1.imprint","IMPRINT",FACE,{"disambiguationData":[TD([[makeQuery(id+"F1.imprint","IMPRINT",EDGE,{"derivedFrom":sQuery(id+"F1.wireOp",EDGE,"E623")}),-1.0]])]});
            extrude(context, id + "F8", {"entities" : qUnion([Q0]), "depth" : 60 * mm});
        }
        {
            var Q0;
            Q0=makeQuery(id+"F1.imprint","IMPRINT",FACE,{"disambiguationData":[TD([[makeQuery(id+"F1.imprint","IMPRINT",EDGE,{"derivedFrom":sQuery(id+"F1.wireOp",EDGE,"E626")}),1.0]])]});
            extrude(context, id + "F9", {"entities" : qUnion([Q0]), "depth" : 60 * mm});
        }
        {
            var Q0;
            Q0=makeQuery(id+"F1.imprint","IMPRINT",FACE,{"disambiguationData":[TD([[makeQuery(id+"F1.imprint","IMPRINT",EDGE,{"derivedFrom":sQuery(id+"F1.wireOp",EDGE,"E128")}),1.0]])]});
            extrude(context, id + "F10", {"entities" : qUnion([Q0]), "depth" : 60 * mm});
        }
        {
            var Q0;
            Q0=makeQuery(id+"F1.imprint","IMPRINT",FACE,{"disambiguationData":[TD([[makeQuery(id+"F1.imprint","IMPRINT",EDGE,{"derivedFrom":sQuery(id+"F1.wireOp",EDGE,"E127")}),1.0]])]});
            extrude(context, id + "F11", {"entities" : qUnion([Q0]), "depth" : 60 * mm});
        }
        {
            var Q0;
            Q0=makeQuery(id+"F1.imprint","IMPRINT",FACE,{"disambiguationData":[TD([[makeQuery(id+"F1.imprint","IMPRINT",EDGE,{"derivedFrom":sQuery(id+"F1.wireOp",EDGE,"E129")}),1.0]])]});
            extrude(context, id + "F12", {"entities" : qUnion([Q0]), "depth" : 60 * mm});
        }
        {
            var Q0;
            Q0=makeQuery(id+"F1.imprint","IMPRINT",FACE,{"disambiguationData":[TD([[makeQuery(id+"F1.imprint","IMPRINT",EDGE,{"derivedFrom":sQuery(id+"F1.wireOp",EDGE,"E131")}),-1.0]])]});
            extrude(context, id + "F13", {"entities" : qUnion([Q0]), "depth" : 60 * mm});
        }
        {
            var Q0;
            {var subQ0=sQuery(id+"F1.wireOp",EDGE,"E644");Q0=makeQuery(id+"F1.imprint","IMPRINT",FACE,{"disambiguationData":[TD([[makeQuery(id+"F1.imprint","IMPRINT",EDGE,{"derivedFrom":subQ0}),-1.0]])]});}
            extrude(context, id + "F14", {"entities" : qUnion([Q0]), "depth" : 60 * mm});
        }
        {
            var Q0;
            Q0=makeQuery(id+"F1.imprint","IMPRINT",FACE,{"disambiguationData":[TD([[makeQuery(id+"F1.imprint","IMPRINT",EDGE,{"derivedFrom":sQuery(id+"F1.wireOp",EDGE,"E643")}),1.0]])]});
            extrude(context, id + "F15", {"entities" : qUnion([Q0]), "depth" : 60 * mm});
        }
        {
            var Q0;
            Q0=makeQuery(id+"F0.imprint","IMPRINT",FACE,{"disambiguationData":[TD([[makeQuery(id+"F0.imprint","IMPRINT",EDGE,{"derivedFrom":sQuery(id+"F0.wireOp",EDGE,"E0")}),-1.0]])]});
            extrude(context, id + "F16", {"entities" : qUnion([Q0]), "depth" : 60 * mm});
        }
        {
            var Q0;
            Q0=makeQuery(id+"F0.imprint","IMPRINT",FACE,{"disambiguationData":[TD([[makeQuery(id+"F0.imprint","IMPRINT",EDGE,{"derivedFrom":sQuery(id+"F0.wireOp",EDGE,"E0")}),1.0]])]});
            extrude(context, id + "F17", {"entities" : qUnion([Q0]), "depth" : 50 * mm});
        }
    });
